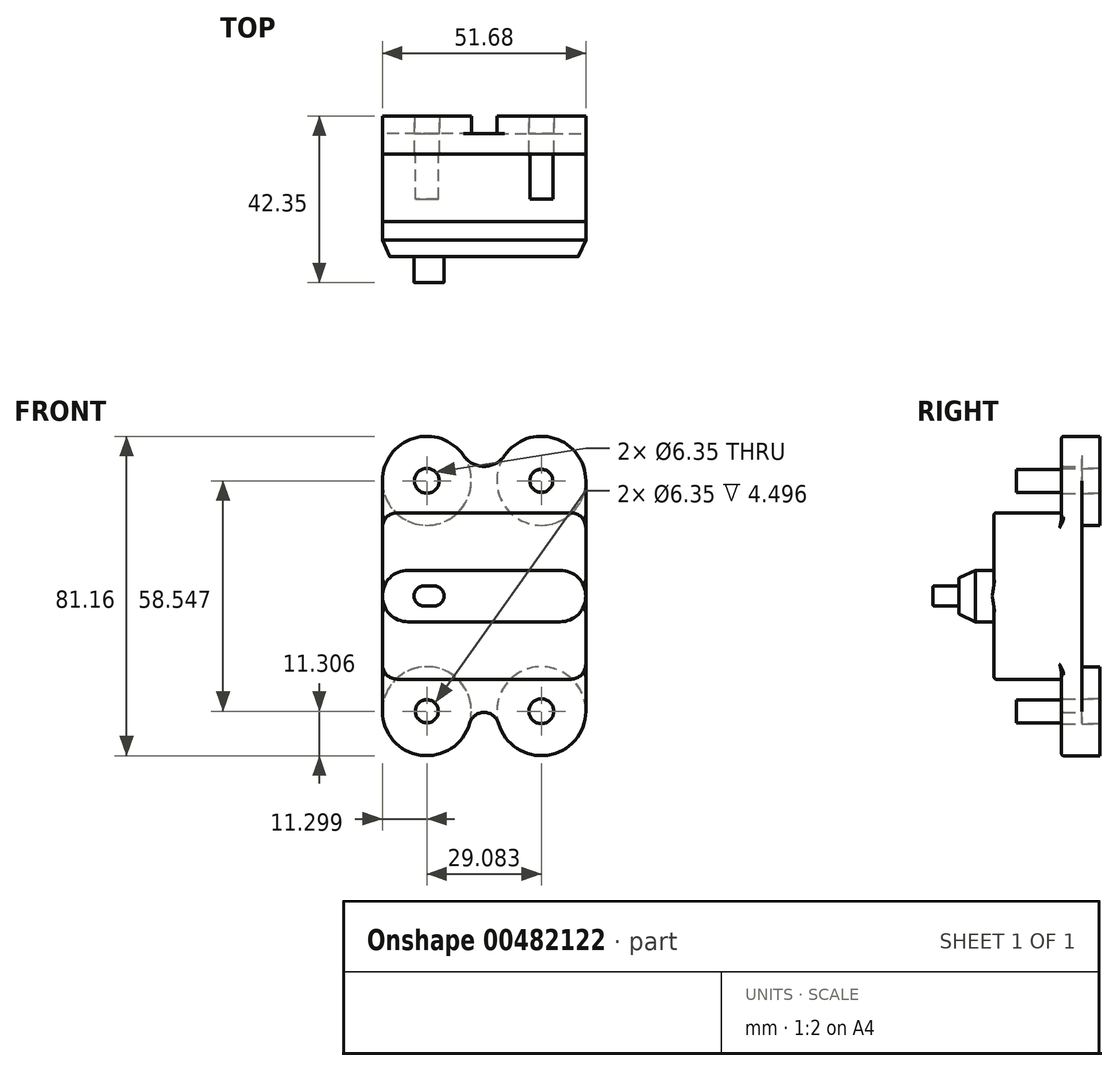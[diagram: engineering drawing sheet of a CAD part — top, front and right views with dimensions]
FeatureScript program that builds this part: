
annotation { "Feature Type Name" : "Feature", "Feature Type Description" : "" }
export const myFeature = defineFeature(function(context is Context, id is Id, definition is map)
    precondition{}
    {
        {
            var Q0;
            Q0=qCreatedBy(makeId("Front.planeOp"),FACE);
            var sketch = newSketch(context, id + "F0", { "sketchPlane" : qUnion([Q0])});
            skLineSegment(sketch, "E0.left", {"start": v(-25.84, 29.27) * mm, "end": v(-25.84, -29.27) * mm});
            skLineSegment(sketch, "E0.right", {"start": v(25.84, 29.27) * mm, "end": v(25.84, -29.27) * mm});
            skPoint(sketch, "E0.middle", {"position": v(0, 0) * mm});
            skLineSegment(sketch, "E1.bottom", {"start": v(-14.54, 29.27) * mm, "end": v(14.54, 29.27) * mm, "construction": true});
            skLineSegment(sketch, "E1.top", {"start": v(-14.54, -29.27) * mm, "end": v(14.54, -29.27) * mm, "construction": true});
            skLineSegment(sketch, "E1.left", {"start": v(-14.54, 29.27) * mm, "end": v(-14.54, -29.27) * mm, "construction": true});
            skLineSegment(sketch, "E1.right", {"start": v(14.54, 29.27) * mm, "end": v(14.54, -29.27) * mm, "construction": true});
            skCircle(sketch, "E2", {"center": v(-14.54, 29.27) * mm, "radius": 3.18 * mm});
            skCircle(sketch, "E3", {"center": v(14.54, -29.27) * mm, "radius": 3.18 * mm});
            skPoint(sketch, "E4.orphan", {"position": v(25.84, 40.58) * mm});
            skPoint(sketch, "E0.bottom.start.orphan", {"position": v(-25.84, 40.58) * mm});
            skPoint(sketch, "E5.orphan", {"position": v(25.84, -40.58) * mm});
            skPoint(sketch, "E6.orphan", {"position": v(-25.84, -40.58) * mm});
            skArc(sketch, "E7", {"start": v(25.84, 29.27) * mm, "mid": v(17.9, 40.07) * mm, "end": v(5.23, 35.68) * mm});
            skArc(sketch, "E8", {"start": v(-5.23, 35.68) * mm, "mid": v(-17.9, 40.07) * mm, "end": v(-25.84, 29.27) * mm});
            skArc(sketch, "E9.filletArc", {"start": v(-5.23, 35.68) * mm, "mid": v(0, 32.93) * mm, "end": v(5.23, 35.68) * mm});
            skArc(sketch, "E10", {"start": v(3.67, -32.35) * mm, "mid": v(16.1, -40.47) * mm, "end": v(25.84, -29.27) * mm});
            skArc(sketch, "E11", {"start": v(-25.84, -29.27) * mm, "mid": v(-16.1, -40.47) * mm, "end": v(-3.67, -32.35) * mm});
            skArc(sketch, "E12.filletArc", {"start": v(3.67, -32.35) * mm, "mid": v(0, -29.58) * mm, "end": v(-3.67, -32.35) * mm});
            skSolve(sketch);
        }
        {
            var Q0;
            Q0 = qSketchRegion(id + "F0", true);
            extrude(context, id + "F1", {"entities" : qUnion([Q0]), "depth" : 5.2 * mm});
        }
        {
            var Q0;
            Q0=makeQuery(id+"F1.opExtrude","CAP_FACE",FACE,{"disambiguationData":[OSD([sQuery(id+"F0.wireOp",EDGE,"E0.left"),sQuery(id+"F0.wireOp",EDGE,"E0.right"),sQuery(id+"F0.wireOp",EDGE,"E2"),sQuery(id+"F0.wireOp",EDGE,"E3"),sQuery(id+"F0.wireOp",EDGE,"E7"),sQuery(id+"F0.wireOp",EDGE,"E8"),sQuery(id+"F0.wireOp",EDGE,"E9.filletArc"),sQuery(id+"F0.wireOp",EDGE,"E10"),sQuery(id+"F0.wireOp",EDGE,"E11"),sQuery(id+"F0.wireOp",EDGE,"E12.filletArc")])],"isStart":true});
            var sketch = newSketch(context, id + "F2", { "sketchPlane" : qUnion([Q0])});
            skCircle(sketch, "E13", {"center": v(-14.54, 29.27) * mm, "radius": 11.3 * mm});
            skCircle(sketch, "E14", {"center": v(14.54, 29.27) * mm, "radius": 11.3 * mm});
            skCircle(sketch, "E15", {"center": v(-14.54, -29.27) * mm, "radius": 11.3 * mm});
            skCircle(sketch, "E16", {"center": v(14.54, -29.27) * mm, "radius": 11.3 * mm});
            skCircle(sketch, "E17", {"center": v(-14.54, 29.27) * mm, "radius": 3.18 * mm});
            skCircle(sketch, "E18", {"center": v(14.54, -29.27) * mm, "radius": 3.18 * mm});
            skCircle(sketch, "E19.0", {"center": v(14.54, 29.27) * mm, "radius": 3.18 * mm});
            skCircle(sketch, "E20.0", {"center": v(-14.54, -29.27) * mm, "radius": 3.18 * mm});
            skSolve(sketch);
        }
        {
            var Q0;
            Q0 = qSketchRegion(id + "F2", true);
            extrude(context, id + "F3", {"entities" : qUnion([Q0]), "operationType" : NewBodyOperationType.ADD, "depth" : 4.5 * mm});
        }
        {
            var Q0;
            Q0=makeQuery(id+"F1.opExtrude","CAP_FACE",FACE,{"disambiguationData":[OSD([sQuery(id+"F0.wireOp",EDGE,"E0.left"),sQuery(id+"F0.wireOp",EDGE,"E0.right"),sQuery(id+"F0.wireOp",EDGE,"E2"),sQuery(id+"F0.wireOp",EDGE,"E3"),sQuery(id+"F0.wireOp",EDGE,"E7"),sQuery(id+"F0.wireOp",EDGE,"E8"),sQuery(id+"F0.wireOp",EDGE,"E9.filletArc"),sQuery(id+"F0.wireOp",EDGE,"E10"),sQuery(id+"F0.wireOp",EDGE,"E11"),sQuery(id+"F0.wireOp",EDGE,"E12.filletArc")])],"isStart":false});
            var sketch = newSketch(context, id + "F4", { "sketchPlane" : qUnion([Q0])});
            skCircle(sketch, "E21", {"center": v(14.54, 29.27) * mm, "radius": 2.92 * mm});
            skCircle(sketch, "E22", {"center": v(-14.54, -29.27) * mm, "radius": 2.92 * mm});
            skSolve(sketch);
        }
        {
            var Q0;
            Q0 = qSketchRegion(id + "F4", true);
            extrude(context, id + "F5", {"entities" : qUnion([Q0]), "operationType" : NewBodyOperationType.ADD, "depth" : 11.43 * mm});
        }
        {
            var Q0;
            Q0=makeQuery(id+"F1.opExtrude","CAP_FACE",FACE,{"disambiguationData":[OSD([sQuery(id+"F0.wireOp",EDGE,"E0.left"),sQuery(id+"F0.wireOp",EDGE,"E0.right"),sQuery(id+"F0.wireOp",EDGE,"E2"),sQuery(id+"F0.wireOp",EDGE,"E3"),sQuery(id+"F0.wireOp",EDGE,"E7"),sQuery(id+"F0.wireOp",EDGE,"E8"),sQuery(id+"F0.wireOp",EDGE,"E9.filletArc"),sQuery(id+"F0.wireOp",EDGE,"E10"),sQuery(id+"F0.wireOp",EDGE,"E11"),sQuery(id+"F0.wireOp",EDGE,"E12.filletArc")])],"isStart":false});
            var sketch = newSketch(context, id + "F6", { "sketchPlane" : qUnion([Q0])});
            skLineSegment(sketch, "E23.bottom", {"start": v(-25.84, 21.15) * mm, "end": v(25.84, 21.15) * mm});
            skLineSegment(sketch, "E23.top", {"start": v(-25.84, -21.15) * mm, "end": v(25.84, -21.15) * mm});
            skLineSegment(sketch, "E23.left", {"start": v(-25.84, 21.15) * mm, "end": v(-25.84, -21.15) * mm});
            skLineSegment(sketch, "E23.right", {"start": v(25.84, 21.15) * mm, "end": v(25.84, -21.15) * mm});
            skPoint(sketch, "E23.middle", {"position": v(0, 0) * mm});
            skSolve(sketch);
        }
        {
            var Q0;
            Q0 = qSketchRegion(id + "F6", true);
            extrude(context, id + "F7", {"entities" : qUnion([Q0]), "operationType" : NewBodyOperationType.ADD, "depth" : 17.14 * mm});
        }
        {
            var Q0;
            Q0=makeQuery(id+"F7.opExtrude","SWEPT_EDGE",EDGE,{"disambiguationData":[OSD([sQuery(id+"F0.wireOp",EDGE,"E0.right"),sQuery(id+"F6.wireOp",EDGE,"E23.top"),sQuery(id+"F6.wireOp",EDGE,"E23.right")])]});
            var Q1;
            Q1=makeQuery(id+"F7.opExtrude","SWEPT_EDGE",EDGE,{"disambiguationData":[OSD([sQuery(id+"F0.wireOp",EDGE,"E0.left"),sQuery(id+"F6.wireOp",EDGE,"E23.top"),sQuery(id+"F6.wireOp",EDGE,"E23.left")])]});
            var Q2;
            Q2=makeQuery(id+"F7.opExtrude","SWEPT_EDGE",EDGE,{"disambiguationData":[OSD([sQuery(id+"F0.wireOp",EDGE,"E0.right"),sQuery(id+"F6.wireOp",EDGE,"E23.bottom"),sQuery(id+"F6.wireOp",EDGE,"E23.right")])]});
            var Q3;
            Q3=makeQuery(id+"F7.opExtrude","SWEPT_EDGE",EDGE,{"disambiguationData":[OSD([sQuery(id+"F0.wireOp",EDGE,"E0.left"),sQuery(id+"F6.wireOp",EDGE,"E23.bottom"),sQuery(id+"F6.wireOp",EDGE,"E23.left")])]});
            fillet(context, id + "F8", {"entities" : qUnion([Q0, Q1, Q2, Q3]), "radius" : 3.8 * mm, "tangentPropagation" : true, "allowEdgeOverflow" : false});
        }
        {
            var Q0;
            Q0=makeQuery(id+"F7.opExtrude","CAP_FACE",FACE,{"disambiguationData":[OSD([sQuery(id+"F6.wireOp",EDGE,"E23.bottom"),sQuery(id+"F6.wireOp",EDGE,"E23.top"),sQuery(id+"F6.wireOp",EDGE,"E23.left"),sQuery(id+"F6.wireOp",EDGE,"E23.right")])],"isStart":false});
            var sketch = newSketch(context, id + "F9", { "sketchPlane" : qUnion([Q0])});
            skLineSegment(sketch, "E24.bottom", {"start": v(-25.84, 6.54) * mm, "end": v(25.84, 6.54) * mm});
            skLineSegment(sketch, "E24.top", {"start": v(-25.84, -6.54) * mm, "end": v(25.84, -6.54) * mm});
            skLineSegment(sketch, "E24.left", {"start": v(-25.84, 6.54) * mm, "end": v(-25.84, -6.54) * mm});
            skLineSegment(sketch, "E24.right", {"start": v(25.84, 6.54) * mm, "end": v(25.84, -6.54) * mm});
            skPoint(sketch, "E24.middle", {"position": v(0, 0) * mm});
            skSolve(sketch);
        }
        {
            var Q0;
            Q0 = qSketchRegion(id + "F9", true);
            extrude(context, id + "F10", {"entities" : qUnion([Q0]), "operationType" : NewBodyOperationType.ADD, "depth" : 8.9 * mm});
        }
        {
            var Q0;
            Q0=makeQuery(id+"F10.opExtrude","SWEPT_EDGE",EDGE,{"disambiguationData":[OSD([sQuery(id+"F6.wireOp",EDGE,"E23.right"),sQuery(id+"F9.wireOp",EDGE,"E24.top"),sQuery(id+"F9.wireOp",EDGE,"E24.right")])]});
            var Q1;
            Q1=makeQuery(id+"F10.opExtrude","SWEPT_EDGE",EDGE,{"disambiguationData":[OSD([sQuery(id+"F6.wireOp",EDGE,"E23.right"),sQuery(id+"F9.wireOp",EDGE,"E24.bottom"),sQuery(id+"F9.wireOp",EDGE,"E24.right")])]});
            var Q2;
            Q2=makeQuery(id+"F10.opExtrude","SWEPT_EDGE",EDGE,{"disambiguationData":[OSD([sQuery(id+"F6.wireOp",EDGE,"E23.left"),sQuery(id+"F9.wireOp",EDGE,"E24.top"),sQuery(id+"F9.wireOp",EDGE,"E24.left")])]});
            var Q3;
            Q3=makeQuery(id+"F10.opExtrude","SWEPT_EDGE",EDGE,{"disambiguationData":[OSD([sQuery(id+"F6.wireOp",EDGE,"E23.left"),sQuery(id+"F9.wireOp",EDGE,"E24.bottom"),sQuery(id+"F9.wireOp",EDGE,"E24.left")])]});
            fillet(context, id + "F11", {"entities" : qUnion([Q0, Q1, Q2, Q3]), "radius" : 6.53 * mm, "tangentPropagation" : true, "allowEdgeOverflow" : false});
        }
        {
            var Q0;
            Q0=makeQuery(id+"F10.opExtrude","CAP_FACE",FACE,{"disambiguationData":[OSD([sQuery(id+"F9.wireOp",EDGE,"E24.bottom"),sQuery(id+"F9.wireOp",EDGE,"E24.top"),sQuery(id+"F9.wireOp",EDGE,"E24.left"),sQuery(id+"F9.wireOp",EDGE,"E24.right")])],"isStart":false});
            chamfer(context, id + "F12", {"entities" : qUnion([Q0]), "chamferType" : ChamferType.TWO_OFFSETS, "width1" : 1.9 * mm, "oppositeDirection" : false, "width2" : 4.2 * mm, "tangentPropagation" : true});
        }
        {
            var Q0;
            {var subQ0=sQuery(id+"F6.wireOp",EDGE,"E23.top");var subQ2=sQuery(id+"F6.wireOp",EDGE,"E23.left");var subQ4=sQuery(id+"F6.wireOp",EDGE,"E23.right");Q0=makeQuery(id+"F10.boolean.opBoolean","SPLIT",FACE,{"disambiguationData":[TD([makeQuery(id+"F7.opExtrude","SWEPT_FACE",FACE,{"disambiguationData":[OSD([subQ0])]})])],"derivedFrom":makeQuery(id+"F7.opExtrude","CAP_FACE",FACE,{"disambiguationData":[OSD([sQuery(id+"F6.wireOp",EDGE,"E23.bottom"),subQ0,subQ2,subQ4])],"isStart":false})});}
            var Q1;
            {var subQ0=sQuery(id+"F6.wireOp",EDGE,"E23.bottom");var subQ3=sQuery(id+"F6.wireOp",EDGE,"E23.left");var subQ4=sQuery(id+"F6.wireOp",EDGE,"E23.right");Q1=makeQuery(id+"F10.boolean.opBoolean","SPLIT",FACE,{"disambiguationData":[TD([makeQuery(id+"F7.opExtrude","SWEPT_FACE",FACE,{"disambiguationData":[OSD([subQ0])]})])],"derivedFrom":makeQuery(id+"F7.opExtrude","CAP_FACE",FACE,{"disambiguationData":[OSD([subQ0,sQuery(id+"F6.wireOp",EDGE,"E23.top"),subQ3,subQ4])],"isStart":false})});}
            fillet(context, id + "F13", {"entities" : qUnion([Q0, Q1]), "radius" : 0.5 * mm, "tangentPropagation" : true, "allowEdgeOverflow" : false});
        }
        {
            var Q0;
            {var subQ0=sQuery(id+"F0.wireOp",EDGE,"E11");var subQ1=sQuery(id+"F0.wireOp",EDGE,"E12.filletArc");var subQ2=sQuery(id+"F0.wireOp",EDGE,"E0.left");var subQ3=sQuery(id+"F0.wireOp",EDGE,"E3");var subQ4=sQuery(id+"F0.wireOp",EDGE,"E0.right");var subQ5=sQuery(id+"F0.wireOp",EDGE,"E10");Q0=makeQuery(id+"F7.boolean.opBoolean","SPLIT",FACE,{"disambiguationData":[TD([makeQuery(id+"F1.opExtrude","SWEPT_FACE",FACE,{"disambiguationData":[OSD([subQ3])]})])],"derivedFrom":makeQuery(id+"F1.opExtrude","CAP_FACE",FACE,{"disambiguationData":[OSD([subQ2,subQ4,sQuery(id+"F0.wireOp",EDGE,"E2"),subQ3,sQuery(id+"F0.wireOp",EDGE,"E7"),sQuery(id+"F0.wireOp",EDGE,"E8"),sQuery(id+"F0.wireOp",EDGE,"E9.filletArc"),subQ5,subQ0,subQ1])],"isStart":false})});}
            var Q1;
            {var subQ0=sQuery(id+"F0.wireOp",EDGE,"E2");var subQ1=sQuery(id+"F0.wireOp",EDGE,"E9.filletArc");var subQ2=sQuery(id+"F0.wireOp",EDGE,"E8");var subQ3=sQuery(id+"F0.wireOp",EDGE,"E0.left");var subQ4=sQuery(id+"F0.wireOp",EDGE,"E0.right");var subQ5=sQuery(id+"F0.wireOp",EDGE,"E7");Q1=makeQuery(id+"F7.boolean.opBoolean","SPLIT",FACE,{"disambiguationData":[TD([makeQuery(id+"F1.opExtrude","SWEPT_FACE",FACE,{"disambiguationData":[OSD([subQ0])]})])],"derivedFrom":makeQuery(id+"F1.opExtrude","CAP_FACE",FACE,{"disambiguationData":[OSD([subQ3,subQ4,subQ0,sQuery(id+"F0.wireOp",EDGE,"E3"),subQ5,subQ2,subQ1,sQuery(id+"F0.wireOp",EDGE,"E10"),sQuery(id+"F0.wireOp",EDGE,"E11"),sQuery(id+"F0.wireOp",EDGE,"E12.filletArc")])],"isStart":false})});}
            fillet(context, id + "F14", {"entities" : qUnion([Q0, Q1]), "radius" : 0.5 * mm, "tangentPropagation" : true, "allowEdgeOverflow" : false});
        }
        {
            var Q0;
            Q0=makeQuery(id+"F10.opExtrude","CAP_FACE",FACE,{"disambiguationData":[OSD([sQuery(id+"F9.wireOp",EDGE,"E24.bottom"),sQuery(id+"F9.wireOp",EDGE,"E24.top"),sQuery(id+"F9.wireOp",EDGE,"E24.left"),sQuery(id+"F9.wireOp",EDGE,"E24.right")])],"isStart":false});
            var sketch = newSketch(context, id + "F15", { "sketchPlane" : qUnion([Q0])});
            skLineSegment(sketch, "E25.bottom", {"start": v(-17.78, -2.54) * mm, "end": v(-10.16, -2.54) * mm});
            skLineSegment(sketch, "E25.top", {"start": v(-17.78, 2.54) * mm, "end": v(-10.16, 2.54) * mm});
            skLineSegment(sketch, "E25.left", {"start": v(-17.78, -2.54) * mm, "end": v(-17.78, 2.54) * mm});
            skLineSegment(sketch, "E25.right", {"start": v(-10.16, -2.54) * mm, "end": v(-10.16, 2.54) * mm});
            skLineSegment(sketch, "E26", {"start": v(-10.16, 0) * mm, "end": v(0, 0) * mm, "construction": true});
            skSolve(sketch);
        }
        {
            var Q0;
            Q0 = qSketchRegion(id + "F15", true);
            extrude(context, id + "F16", {"entities" : qUnion([Q0]), "operationType" : NewBodyOperationType.ADD, "depth" : 6.6 * mm});
        }
        {
            var Q0;
            Q0=makeQuery(id+"F16.opExtrude","SWEPT_EDGE",EDGE,{"disambiguationData":[OSD([sQuery(id+"F15.wireOp",EDGE,"E25.bottom"),sQuery(id+"F15.wireOp",EDGE,"E25.right")])]});
            var Q1;
            Q1=makeQuery(id+"F16.opExtrude","SWEPT_EDGE",EDGE,{"disambiguationData":[OSD([sQuery(id+"F15.wireOp",EDGE,"E25.top"),sQuery(id+"F15.wireOp",EDGE,"E25.right")])]});
            var Q2;
            Q2=makeQuery(id+"F16.opExtrude","SWEPT_EDGE",EDGE,{"disambiguationData":[OSD([sQuery(id+"F15.wireOp",EDGE,"E25.bottom"),sQuery(id+"F15.wireOp",EDGE,"E25.left")])]});
            var Q3;
            Q3=makeQuery(id+"F16.opExtrude","SWEPT_EDGE",EDGE,{"disambiguationData":[OSD([sQuery(id+"F15.wireOp",EDGE,"E25.top"),sQuery(id+"F15.wireOp",EDGE,"E25.left")])]});
            fillet(context, id + "F17", {"entities" : qUnion([Q0, Q1, Q2, Q3]), "radius" : 2.54 * mm, "tangentPropagation" : true, "allowEdgeOverflow" : false});
        }
        {
            var Q0;
            Q0=makeQuery(id+"F16.opExtrude","CAP_FACE",FACE,{"disambiguationData":[OSD([sQuery(id+"F15.wireOp",EDGE,"E25.bottom"),sQuery(id+"F15.wireOp",EDGE,"E25.top"),sQuery(id+"F15.wireOp",EDGE,"E25.left"),sQuery(id+"F15.wireOp",EDGE,"E25.right")])],"isStart":false});
            var Q1;
            Q1=makeQuery(id+"F10.opExtrude","CAP_FACE",FACE,{"disambiguationData":[OSD([sQuery(id+"F9.wireOp",EDGE,"E24.bottom"),sQuery(id+"F9.wireOp",EDGE,"E24.top"),sQuery(id+"F9.wireOp",EDGE,"E24.left"),sQuery(id+"F9.wireOp",EDGE,"E24.right")])],"isStart":false});
            fillet(context, id + "F18", {"entities" : qUnion([Q0, Q1]), "radius" : 0.25 * mm, "tangentPropagation" : true, "allowEdgeOverflow" : false});
        }
    });
